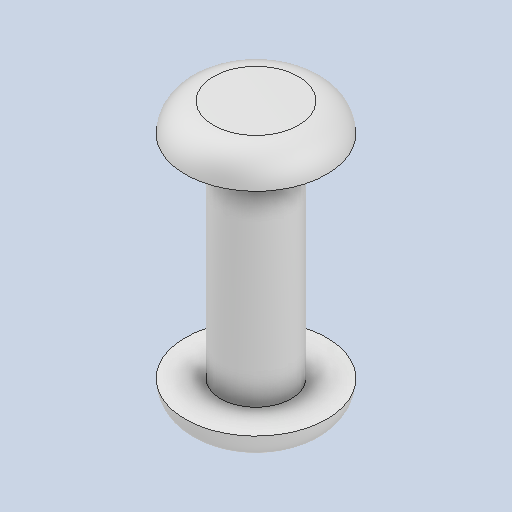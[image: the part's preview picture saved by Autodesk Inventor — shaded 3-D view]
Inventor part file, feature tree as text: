
AUTODESK INVENTOR PART (.ipt)
format: ipt  version: 2024.2 (Build 282272000, 272)  size: 142,336 bytes
history: native  units: mm
features: extrude x3, other x1, sketch x1, fillet x1
ambient origin geometry x8: Origin, YZ Plane, XZ Plane, XY Plane, X Axis, Y Axis, Z Axis, Center Point
bodies: Body1 (feature_tree)
feature tree (6):
  other  "Bryła1"
  sketch  "Szkic1"
  extrude  "Wyciągnięcie proste1"  Depth=5.0mm
  extrude  "Wyciągnięcie proste2"  Depth=10.0mm
  extrude  "Wyciągnięcie proste3"  Depth=2.0mm TaperAngle=0.0deg
  fillet  "Zaokrąglenie1"  Radius=17.0mm
